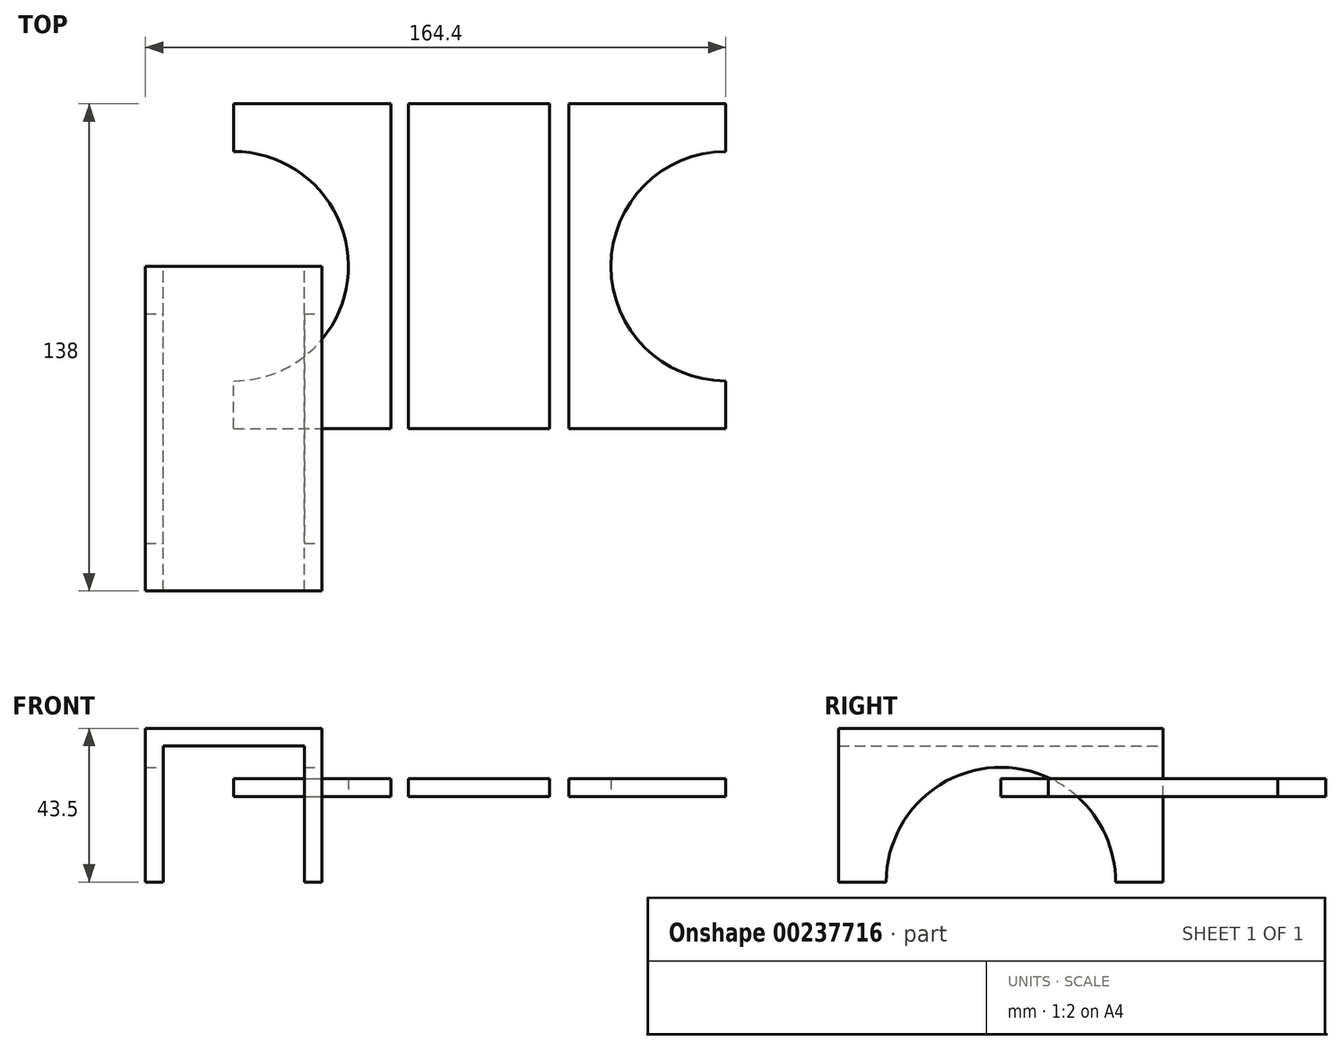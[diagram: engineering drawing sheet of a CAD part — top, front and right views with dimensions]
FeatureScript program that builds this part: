
annotation { "Feature Type Name" : "Feature", "Feature Type Description" : "" }
export const myFeature = defineFeature(function(context is Context, id is Id, definition is map)
    precondition{}
    {
        {
            var Q0;
            Q0=qCreatedBy(makeId("Front.planeOp"),FACE);
            var sketch = newSketch(context, id + "F0", { "sketchPlane" : qUnion([Q0])});
            skLineSegment(sketch, "E0.top", {"start": v(25, 19.25) * mm, "end": v(-25, 19.25) * mm});
            skLineSegment(sketch, "E0.left", {"start": v(25, -24.25) * mm, "end": v(25, 19.25) * mm});
            skLineSegment(sketch, "E0.right", {"start": v(-25, -24.25) * mm, "end": v(-25, 19.25) * mm});
            skLineSegment(sketch, "E1", {"start": v(-25, -24.25) * mm, "end": v(-20, -24.25) * mm});
            skLineSegment(sketch, "E2", {"start": v(-20, -24.25) * mm, "end": v(-20, 14.25) * mm});
            skLineSegment(sketch, "E3", {"start": v(-20, 14.25) * mm, "end": v(20, 14.25) * mm});
            skLineSegment(sketch, "E4", {"start": v(20, 14.25) * mm, "end": v(20, -24.25) * mm});
            skLineSegment(sketch, "E5", {"start": v(20, -24.25) * mm, "end": v(25, -24.25) * mm});
            skSolve(sketch);
        }
        {
            var Q0;
            Q0=makeQuery(id+"F0.imprint","IMPRINT",FACE,{"disambiguationData":[TD([[makeQuery(id+"F0.imprint","IMPRINT",EDGE,{"derivedFrom":sQuery(id+"F0.wireOp",EDGE,"E0.top")}),1.0]])]});
            extrude(context, id + "F1", {"entities" : qUnion([Q0]), "endBound" : BoundingType.SYMMETRIC, "depth" : 92 * mm});
        }
        {
            var Q0;
            Q0=makeQuery(id+"F1.opExtrude","SWEPT_FACE",FACE,{"disambiguationData":[OSD([sQuery(id+"F0.wireOp",EDGE,"E0.left")])]});
            var sketch = newSketch(context, id + "F2", { "sketchPlane" : qUnion([Q0])});
            skCircle(sketch, "E6", {"center": v(0, -24.25) * mm, "radius": 32.5 * mm});
            skSolve(sketch);
        }
        {
            var Q0;
            {var subQ0=sQuery(id+"F2.wireOp",EDGE,"E6");var subQ1=makeQuery(id+"F1.opExtrude","SWEPT_EDGE",EDGE,{"disambiguationData":[OSD([sQuery(id+"F0.wireOp",EDGE,"E0.left"),sQuery(id+"F0.wireOp",EDGE,"E5")])]});var subQ2=makeQuery(id+"F2.imprint","INTERSECT",VERTEX,{"disambiguationData":[OD(0.0)],"derivedFrom":[subQ1,subQ0]});Q0=makeQuery(id+"F2.imprint","IMPRINT",FACE,{"disambiguationData":[TD([[makeQuery(id+"F2.imprint","IMPRINT",EDGE,{"disambiguationData":[TD([[subQ2,-1.0]])],"derivedFrom":subQ0}),1.0]])]});}
            extrude(context, id + "F3", {"entities" : qUnion([Q0]), "operationType" : NewBodyOperationType.REMOVE, "oppositeDirection" : true, "depth" : 54 * mm});
        }
        {
            var Q0;
            Q0=qCreatedBy(makeId("Top.planeOp"),FACE);
            var sketch = newSketch(context, id + "F4", { "sketchPlane" : qUnion([Q0])});
            skLineSegment(sketch, "E7.bottom", {"start": v(0, 0) * mm, "end": v(44.5, 0) * mm});
            skLineSegment(sketch, "E7.top", {"start": v(0, 92) * mm, "end": v(44.5, 92) * mm});
            skLineSegment(sketch, "E7.left", {"start": v(0, 0) * mm, "end": v(0, 13.5) * mm});
            skLineSegment(sketch, "E7.right", {"start": v(139.4, 0) * mm, "end": v(139.4, 13.5) * mm});
            skLineSegment(sketch, "E8", {"start": v(44.5, 92) * mm, "end": v(44.5, 0) * mm, "construction": true});
            skLineSegment(sketch, "E9", {"start": v(94.9, 92) * mm, "end": v(94.9, 0) * mm, "construction": true});
            skArc(sketch, "E10", {"start": v(0, 13.5) * mm, "mid": v(32.5, 46) * mm, "end": v(0, 78.5) * mm});
            skArc(sketch, "E11", {"start": v(139.4, 78.5) * mm, "mid": v(106.9, 46) * mm, "end": v(139.4, 13.5) * mm});
            skLineSegment(sketch, "E12.trimOffspring", {"start": v(0, 78.5) * mm, "end": v(0, 92) * mm});
            skLineSegment(sketch, "E13.trimOffspring", {"start": v(139.4, 78.5) * mm, "end": v(139.4, 92) * mm});
            skLineSegment(sketch, "E14", {"start": v(89.44, 92) * mm, "end": v(89.44, 0) * mm});
            skLineSegment(sketch, "E15", {"start": v(49.44, 92) * mm, "end": v(49.44, 0) * mm});
            skLineSegment(sketch, "E16.trimOffspring", {"start": v(49.44, 92) * mm, "end": v(89.44, 92) * mm});
            skLineSegment(sketch, "E17.trimOffspring", {"start": v(94.9, 92) * mm, "end": v(139.4, 92) * mm});
            skLineSegment(sketch, "E18.trimOffspring", {"start": v(94.9, 0) * mm, "end": v(139.4, 0) * mm});
            skLineSegment(sketch, "E19.trimOffspring", {"start": v(49.44, 0) * mm, "end": v(89.44, 0) * mm});
            skLineSegment(sketch, "E20", {"start": v(44.5, 92) * mm, "end": v(44.5, 0) * mm});
            skLineSegment(sketch, "E21", {"start": v(94.9, 92) * mm, "end": v(94.9, 0) * mm});
            skSolve(sketch);
        }
        {
            var Q0;
            Q0 = qSketchRegion(id + "F4", true);
            extrude(context, id + "F5", {"entities" : qUnion([Q0]), "depth" : 5 * mm});
        }
    });
